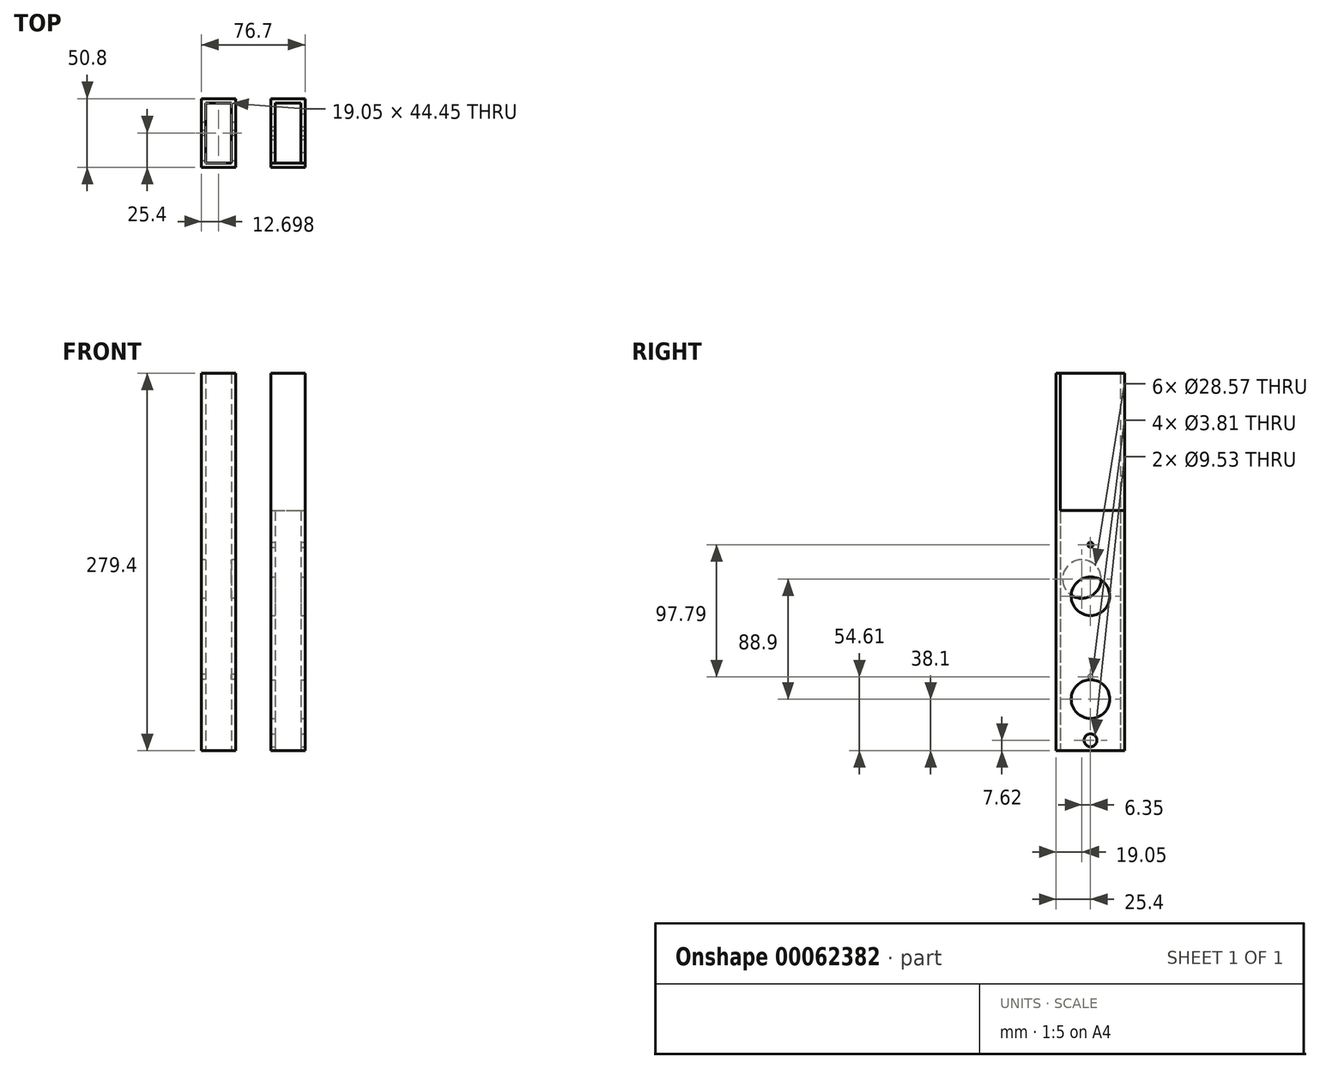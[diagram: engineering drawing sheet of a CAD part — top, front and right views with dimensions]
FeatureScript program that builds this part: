
annotation { "Feature Type Name" : "Feature", "Feature Type Description" : "" }
export const myFeature = defineFeature(function(context is Context, id is Id, definition is map)
    precondition{}
    {
        {
            var Q0;
            Q0=qCreatedBy(makeId("Top.planeOp"),FACE);
            var sketch = newSketch(context, id + "F0", { "sketchPlane" : qUnion([Q0])});
            skLineSegment(sketch, "E0.bottom", {"start": v(0, 0) * mm, "end": v(25.4, 0) * mm});
            skLineSegment(sketch, "E0.top", {"start": v(0, 50.8) * mm, "end": v(25.4, 50.8) * mm});
            skLineSegment(sketch, "E0.left", {"start": v(0, 0) * mm, "end": v(0, 50.8) * mm});
            skLineSegment(sketch, "E0.right", {"start": v(25.4, 0) * mm, "end": v(25.4, 50.8) * mm});
            skLineSegment(sketch, "E1.0", {"start": v(3.17, 3.18) * mm, "end": v(22.23, 3.18) * mm});
            skLineSegment(sketch, "E1.1", {"start": v(3.17, 3.18) * mm, "end": v(3.17, 47.63) * mm});
            skLineSegment(sketch, "E1.2", {"start": v(3.17, 47.63) * mm, "end": v(22.22, 47.63) * mm});
            skLineSegment(sketch, "E1.3", {"start": v(22.23, 3.18) * mm, "end": v(22.22, 47.62) * mm});
            skSolve(sketch);
        }
        {
            var Q0;
            Q0=makeQuery(id+"F0.imprint","IMPRINT",FACE,{"disambiguationData":[TD([[makeQuery(id+"F0.imprint","IMPRINT",EDGE,{"derivedFrom":sQuery(id+"F0.wireOp",EDGE,"E0.bottom")}),1.0]])]});
            extrude(context, id + "F1", {"entities" : qUnion([Q0]), "depth" : 177.8 * mm});
        }
        {
            var Q0;
            Q0=makeQuery(id+"F1.opExtrude","SWEPT_FACE",FACE,{"disambiguationData":[OSD([sQuery(id+"F0.wireOp",EDGE,"E0.right")])]});
            var sketch = newSketch(context, id + "F2", { "sketchPlane" : qUnion([Q0])});
            skCircle(sketch, "E2", {"center": v(25.4, 152.4) * mm, "radius": 1.9 * mm});
            skPoint(sketch, "E2.centerSnap0", {"position": v(25.4, 177.8) * mm});
            skCircle(sketch, "E3", {"center": v(25.4, 38.1) * mm, "radius": 14.29 * mm});
            skPoint(sketch, "E3.centerSnap0", {"position": v(25.4, 0) * mm});
            skCircle(sketch, "E4", {"center": v(25.4, 7.62) * mm, "radius": 4.76 * mm});
            skCircle(sketch, "E5", {"center": v(25.4, 114.3) * mm, "radius": 14.29 * mm});
            skSolve(sketch);
        }
        {
            var Q0;
            Q0=makeQuery(id+"F2.imprint","IMPRINT",FACE,{"disambiguationData":[TD([[makeQuery(id+"F2.imprint","IMPRINT",EDGE,{"derivedFrom":sQuery(id+"F2.wireOp",EDGE,"E2")}),1.0]])]});
            var Q1;
            Q1=makeQuery(id+"F2.imprint","IMPRINT",FACE,{"disambiguationData":[TD([[makeQuery(id+"F2.imprint","IMPRINT",EDGE,{"derivedFrom":sQuery(id+"F2.wireOp",EDGE,"E3")}),1.0]])]});
            var Q2;
            Q2=makeQuery(id+"F2.imprint","IMPRINT",FACE,{"disambiguationData":[TD([[makeQuery(id+"F2.imprint","IMPRINT",EDGE,{"derivedFrom":sQuery(id+"F2.wireOp",EDGE,"E4")}),1.0]])]});
            var Q3;
            Q3=makeQuery(id+"F2.imprint","IMPRINT",FACE,{"disambiguationData":[TD([[makeQuery(id+"F2.imprint","IMPRINT",EDGE,{"derivedFrom":sQuery(id+"F2.wireOp",EDGE,"E5")}),1.0]])]});
            var Q4;
            Q4=makeQuery(id+"F1.opExtrude","SWEPT_FACE",FACE,{"disambiguationData":[OSD([sQuery(id+"F0.wireOp",EDGE,"E0.left")])]});
            extrude(context, id + "F3", {"entities" : qUnion([Q0, Q1, Q2, Q3]), "operationType" : NewBodyOperationType.REMOVE, "endBound" : BoundingType.UP_TO_SURFACE, "oppositeDirection" : true, "endBoundEntityFace" : qUnion([Q4]), "depth" : 25.4 * mm});
        }
        {
            var Q0;
            Q0=qCreatedBy(makeId("Top.planeOp"),FACE);
            var sketch = newSketch(context, id + "F4", { "sketchPlane" : qUnion([Q0])});
            skLineSegment(sketch, "E6.bottom", {"start": v(-25.9, 0) * mm, "end": v(-51.3, 0) * mm});
            skLineSegment(sketch, "E6.top", {"start": v(-25.9, 50.8) * mm, "end": v(-51.3, 50.8) * mm});
            skLineSegment(sketch, "E6.left", {"start": v(-25.9, 0) * mm, "end": v(-25.9, 50.8) * mm});
            skLineSegment(sketch, "E6.right", {"start": v(-51.3, 0) * mm, "end": v(-51.3, 50.8) * mm});
            skLineSegment(sketch, "E7.0", {"start": v(-29.08, 3.18) * mm, "end": v(-48.13, 3.17) * mm});
            skLineSegment(sketch, "E7.1", {"start": v(-29.08, 3.18) * mm, "end": v(-29.08, 47.62) * mm});
            skLineSegment(sketch, "E7.2", {"start": v(-29.08, 47.62) * mm, "end": v(-48.13, 47.62) * mm});
            skLineSegment(sketch, "E7.3", {"start": v(-48.13, 3.17) * mm, "end": v(-48.13, 47.62) * mm});
            skSolve(sketch);
        }
        {
            var Q0;
            Q0=makeQuery(id+"F4.imprint","IMPRINT",FACE,{"disambiguationData":[TD([[makeQuery(id+"F4.imprint","IMPRINT",EDGE,{"derivedFrom":sQuery(id+"F4.wireOp",EDGE,"E6.bottom")}),-1.0]])]});
            extrude(context, id + "F5", {"entities" : qUnion([Q0]), "depth" : 279.4 * mm});
        }
        {
            var Q0;
            Q0=makeQuery(id+"F5.opExtrude","SWEPT_FACE",FACE,{"disambiguationData":[OSD([sQuery(id+"F4.wireOp",EDGE,"E6.right")])]});
            var sketch = newSketch(context, id + "F6", { "sketchPlane" : qUnion([Q0])});
            skPoint(sketch, "E8.centerSnap0", {"position": v(-25.4, 279.4) * mm});
            skCircle(sketch, "E9", {"center": v(-25.4, 54.61) * mm, "radius": 1.9 * mm});
            skSolve(sketch);
        }
        {
            var Q0;
            Q0=makeQuery(id+"F6.imprint","IMPRINT",FACE,{"disambiguationData":[TD([[makeQuery(id+"F6.imprint","IMPRINT",EDGE,{"derivedFrom":sQuery(id+"F6.wireOp",EDGE,"E8")}),1.0]])]});
            var Q1;
            Q1=makeQuery(id+"F6.imprint","IMPRINT",FACE,{"disambiguationData":[TD([[makeQuery(id+"F6.imprint","IMPRINT",EDGE,{"derivedFrom":sQuery(id+"F6.wireOp",EDGE,"E9")}),1.0]])]});
            var Q2;
            Q2=makeQuery(id+"F5.opExtrude","SWEPT_FACE",FACE,{"disambiguationData":[OSD([sQuery(id+"F4.wireOp",EDGE,"E6.left")])]});
            extrude(context, id + "F7", {"entities" : qUnion([Q0, Q1]), "operationType" : NewBodyOperationType.REMOVE, "endBound" : BoundingType.UP_TO_SURFACE, "oppositeDirection" : true, "endBoundEntityFace" : qUnion([Q2]), "depth" : 25.4 * mm});
        }
        {
            var Q0;
            Q0=makeQuery(id+"F5.opExtrude","SWEPT_FACE",FACE,{"disambiguationData":[OSD([sQuery(id+"F4.wireOp",EDGE,"E6.right")])]});
            var sketch = newSketch(context, id + "F8", { "sketchPlane" : qUnion([Q0])});
            skCircle(sketch, "E10", {"center": v(-19.05, 127) * mm, "radius": 14.29 * mm});
            skPoint(sketch, "E10.centerSnap0", {"position": v(-25.4, 279.4) * mm});
            skSolve(sketch);
        }
        {
            var Q0;
            Q0=makeQuery(id+"F8.imprint","IMPRINT",FACE,{"disambiguationData":[TD([[makeQuery(id+"F8.imprint","IMPRINT",EDGE,{"derivedFrom":sQuery(id+"F8.wireOp",EDGE,"E10")}),1.0]])]});
            var Q1;
            Q1=makeQuery(id+"F8.imprint","IMPRINT",FACE,{"disambiguationData":[TD([[makeQuery(id+"F8.imprint","IMPRINT",EDGE,{"derivedFrom":sQuery(id+"F8.wireOp",EDGE,"dafb48fc-ab06-4f12-9454-6807a5b66b07")}),1.0]])]});
            var Q2;
            Q2=makeQuery(id+"F5.opExtrude","SWEPT_FACE",FACE,{"disambiguationData":[OSD([sQuery(id+"F4.wireOp",EDGE,"E6.left")])]});
            extrude(context, id + "F9", {"entities" : qUnion([Q0, Q1]), "operationType" : NewBodyOperationType.REMOVE, "endBound" : BoundingType.UP_TO_SURFACE, "oppositeDirection" : true, "endBoundEntityFace" : qUnion([Q2]), "depth" : 25.4 * mm});
        }
        {
            var Q0;
            Q0=makeQuery(id+"F1.opExtrude","CAP_FACE",FACE,{"disambiguationData":[OSD([sQuery(id+"F0.wireOp",EDGE,"E0.bottom"),sQuery(id+"F0.wireOp",EDGE,"E0.top"),sQuery(id+"F0.wireOp",EDGE,"E0.left"),sQuery(id+"F0.wireOp",EDGE,"E0.right"),sQuery(id+"F0.wireOp",EDGE,"E1.0"),sQuery(id+"F0.wireOp",EDGE,"E1.1"),sQuery(id+"F0.wireOp",EDGE,"E1.2"),sQuery(id+"F0.wireOp",EDGE,"E1.3")])],"isStart":false});
            var sketch = newSketch(context, id + "F10", { "sketchPlane" : qUnion([Q0])});
            skLineSegment(sketch, "E11.bottom", {"start": v(0, 0) * mm, "end": v(25.4, 0) * mm});
            skLineSegment(sketch, "E11.top", {"start": v(0, 3.18) * mm, "end": v(25.4, 3.18) * mm});
            skLineSegment(sketch, "E11.left", {"start": v(0, 0) * mm, "end": v(0, 3.18) * mm});
            skLineSegment(sketch, "E11.right", {"start": v(25.4, 0) * mm, "end": v(25.4, 3.17) * mm});
            skSolve(sketch);
        }
        {
            var Q0;
            Q0=makeQuery(id+"F10.imprint","IMPRINT",FACE,{"disambiguationData":[TD([[makeQuery(id+"F10.imprint","IMPRINT",EDGE,{"derivedFrom":sQuery(id+"F10.wireOp",EDGE,"E11.bottom")}),1.0]])]});
            extrude(context, id + "F11", {"entities" : qUnion([Q0]), "operationType" : NewBodyOperationType.ADD, "depth" : 101.6 * mm});
        }
    });
